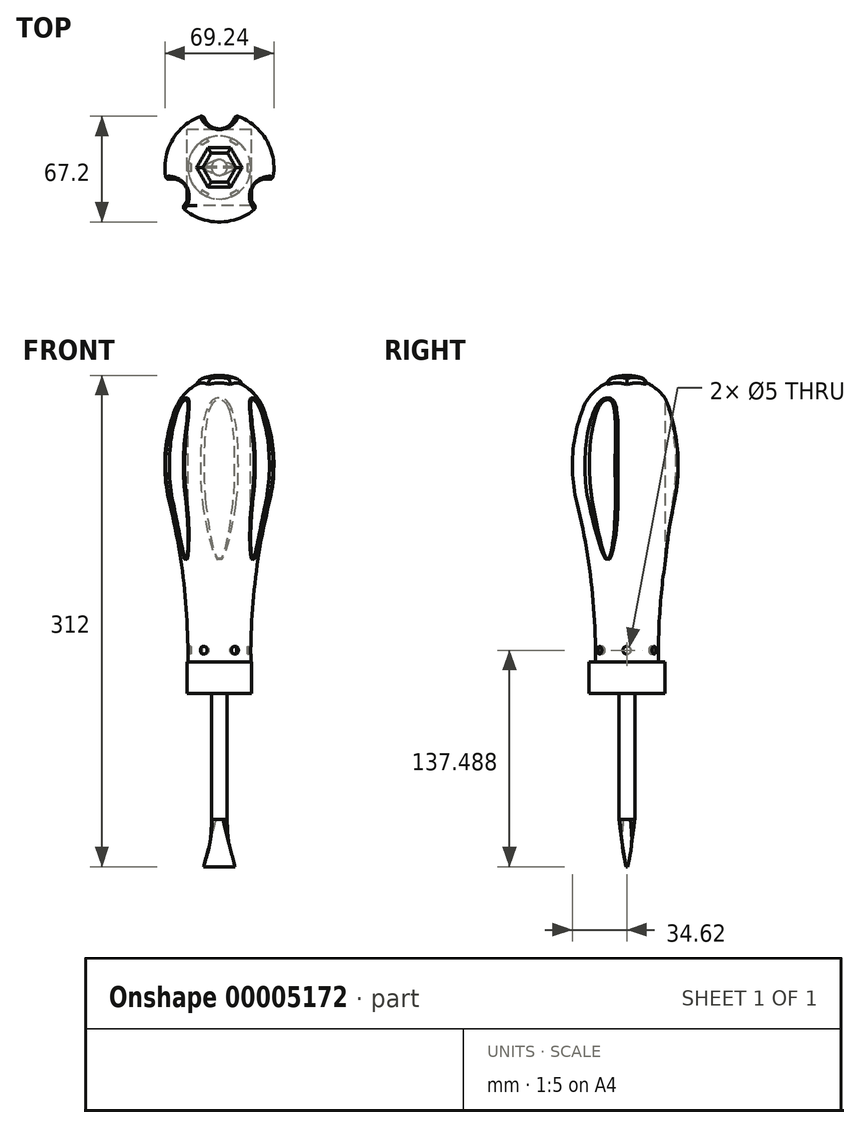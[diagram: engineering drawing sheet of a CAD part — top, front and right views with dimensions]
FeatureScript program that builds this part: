
annotation { "Feature Type Name" : "Feature", "Feature Type Description" : "" }
export const myFeature = defineFeature(function(context is Context, id is Id, definition is map)
    precondition{}
    {
        {
            var Q0;
            Q0=qCreatedBy(makeId("Front.planeOp"),FACE);
            var sketch = newSketch(context, id + "F0", { "sketchPlane" : qUnion([Q0])});
            skLineSegment(sketch, "E0", {"start": v(0, 0) * mm, "end": v(5, 0) * mm});
            skLineSegment(sketch, "E1", {"start": v(5, 0) * mm, "end": v(5, 99.99) * mm});
            skLineSegment(sketch, "E2", {"start": v(5, 99.99) * mm, "end": v(20, 99.99) * mm});
            skLineSegment(sketch, "E3", {"start": v(20, 99.99) * mm, "end": v(20, 104.99) * mm});
            skArc(sketch, "E4", {"start": v(20, 104.99) * mm, "mid": v(22.93, 153.35) * mm, "end": v(31.7, 201) * mm});
            skArc(sketch, "E5", {"start": v(31.7, 201) * mm, "mid": v(34.43, 231.14) * mm, "end": v(28.02, 260.71) * mm});
            skArc(sketch, "E6", {"start": v(28.02, 260.71) * mm, "mid": v(24.7, 267.02) * mm, "end": v(20, 272.36) * mm});
            skLineSegment(sketch, "E7", {"start": v(0, 280) * mm, "end": v(0, 0) * mm});
            skArc(sketch, "E8", {"start": v(20, 274.98) * mm, "mid": v(10.6, 280.2) * mm, "end": v(0, 282) * mm});
            skLineSegment(sketch, "E9", {"start": v(0, 280) * mm, "end": v(0, 282) * mm});
            skLineSegment(sketch, "E10", {"start": v(20, 272.36) * mm, "end": v(20, 274.98) * mm});
            skSolve(sketch);
        }
        {
            var Q0;
            Q0 = qSketchRegion(id + "F0", true);
            var Q1;
            Q1=sQuery(id+"F0.wireOp",EDGE,"E7");
            revolve(context, id + "F1", {"entities" : qUnion([Q0]), "axis" : qUnion([Q1]), "revolveType" : RevolveType.FULL});
        }
        {
            var Q0;
            Q0=qCreatedBy(makeId("Top.planeOp"),FACE);
            cPlane(context, id + "F2", {"entities" : qUnion([Q0]), "cplaneType" : CPlaneType.OFFSET, "offset" : 300 * mm, "width" : 150 * mm, "height" : 150 * mm});
        }
        {
            var Q0;
            Q0=qCreatedBy(id+"F2.planeOp",FACE);
            var sketch = newSketch(context, id + "F3", { "sketchPlane" : qUnion([Q0])});
            skCircle(sketch, "E11.cCircle", {"center": v(0, 0) * mm, "radius": 12.5 * mm, "construction": true});
            skLineSegment(sketch, "E11.0", {"start": v(7.22, 12.5) * mm, "end": v(14.43, 0) * mm});
            skLineSegment(sketch, "E11.1", {"start": v(14.43, 0) * mm, "end": v(7.22, -12.5) * mm});
            skLineSegment(sketch, "E11.2", {"start": v(7.22, -12.5) * mm, "end": v(-7.22, -12.5) * mm});
            skLineSegment(sketch, "E11.3", {"start": v(-7.22, -12.5) * mm, "end": v(-14.43, 0) * mm});
            skLineSegment(sketch, "E11.4", {"start": v(-14.43, 0) * mm, "end": v(-7.22, 12.5) * mm});
            skLineSegment(sketch, "E11.5", {"start": v(-7.22, 12.5) * mm, "end": v(7.22, 12.5) * mm});
            skPoint(sketch, "E11.0.midPoint", {"position": v(10.83, 6.25) * mm});
            skCircle(sketch, "E12.0", {"center": v(0, 0) * mm, "radius": 20 * mm});
            skSolve(sketch);
        }
        {
            var Q0;
            Q0=makeQuery(id+"F3.imprint","IMPRINT",FACE,{"disambiguationData":[TD([[makeQuery(id+"F3.imprint","IMPRINT",EDGE,{"derivedFrom":sQuery(id+"F3.wireOp",EDGE,"E11.0")}),1.0]])]});
            var Q1;
            Q1=makeQuery(id+"F1.opRevolve","SWEPT_FACE",FACE,{"disambiguationData":[OSD([sQuery(id+"F0.wireOp",EDGE,"E6")])]});
            extrude(context, id + "F4", {"entities" : qUnion([Q0]), "operationType" : NewBodyOperationType.REMOVE, "endBound" : BoundingType.UP_TO_SURFACE, "oppositeDirection" : true, "endBoundEntityFace" : qUnion([Q1]), "depth" : 25 * mm});
        }
        {
            var Q0;
            Q0=qCreatedBy(id+"F2.planeOp",FACE);
            var sketch = newSketch(context, id + "F5", { "sketchPlane" : qUnion([Q0])});
            skCircle(sketch, "E13", {"center": v(0, 34.5) * mm, "radius": 10 * mm});
            skSolve(sketch);
        }
        {
            var Q0;
            Q0 = qSketchRegion(id + "F5", true);
            extrude(context, id + "F6", {"entities" : qUnion([Q0]), "endBound" : BoundingType.THROUGH_ALL, "oppositeDirection" : true, "depth" : 25 * mm});
        }
        {
            var Q0;
            Q0=makeQuery(id+"F6.opExtrude","SWEPT_FACE",FACE,{"disambiguationData":[OSD([sQuery(id+"F5.wireOp",EDGE,"E13")])]});
            var Q1;
            Q1=makeQuery(id+"F6.opExtrude","SWEPT_BODY",BODY,{"disambiguationData":[OSD([sQuery(id+"F5.wireOp",EDGE,"E13")])]});
            var Q2;
            Q2=makeQuery(id+"F1.opRevolve","SWEPT_FACE",FACE,{"disambiguationData":[OSD([sQuery(id+"F0.wireOp",EDGE,"E5")])]});
            circularPattern(context, id + "F7", {"entities" : qUnion([Q1]), "axis" : qUnion([Q2]), "angle" : 360 * degree, "instanceCount" : 3, "equalSpace" : true});
        }
        {
            var Q0;
            Q0=makeQuery(id+"F7.opPattern","COPY",BODY,{"derivedFrom":makeQuery(id+"F6.opExtrude","SWEPT_BODY",BODY,{"disambiguationData":[OSD([sQuery(id+"F5.wireOp",EDGE,"E13")])]}),"instanceName":"3"});
            var Q1;
            Q1=makeQuery(id+"F7.opPattern","COPY",BODY,{"derivedFrom":makeQuery(id+"F6.opExtrude","SWEPT_BODY",BODY,{"disambiguationData":[OSD([sQuery(id+"F5.wireOp",EDGE,"E13")])]}),"instanceName":"4"});
            var Q2;
            Q2=makeQuery(id+"F7.opPattern","COPY",BODY,{"derivedFrom":makeQuery(id+"F6.opExtrude","SWEPT_BODY",BODY,{"disambiguationData":[OSD([sQuery(id+"F5.wireOp",EDGE,"E13")])]}),"instanceName":"5"});
            var Q3;
            Q3=makeQuery(id+"F6.opExtrude","SWEPT_BODY",BODY,{"disambiguationData":[OSD([sQuery(id+"F5.wireOp",EDGE,"E13")])]});
            var Q4;
            Q4=makeQuery(id+"F7.opPattern","COPY",BODY,{"derivedFrom":makeQuery(id+"F6.opExtrude","SWEPT_BODY",BODY,{"disambiguationData":[OSD([sQuery(id+"F5.wireOp",EDGE,"E13")])]}),"instanceName":"1"});
            var Q5;
            Q5=makeQuery(id+"F7.opPattern","COPY",BODY,{"derivedFrom":makeQuery(id+"F6.opExtrude","SWEPT_BODY",BODY,{"disambiguationData":[OSD([sQuery(id+"F5.wireOp",EDGE,"E13")])]}),"instanceName":"2"});
            var Q6;
            Q6=makeQuery(id+"F1.opRevolve","SWEPT_BODY",BODY,{"disambiguationData":[OSD([sQuery(id+"F0.wireOp",EDGE,"E0"),sQuery(id+"F0.wireOp",EDGE,"E1"),sQuery(id+"F0.wireOp",EDGE,"E2"),sQuery(id+"F0.wireOp",EDGE,"E3"),sQuery(id+"F0.wireOp",EDGE,"E4"),sQuery(id+"F0.wireOp",EDGE,"E5"),sQuery(id+"F0.wireOp",EDGE,"E6"),sQuery(id+"F0.wireOp",EDGE,"E7"),sQuery(id+"F0.wireOp",EDGE,"E8"),sQuery(id+"F0.wireOp",EDGE,"E9"),sQuery(id+"F0.wireOp",EDGE,"E10")])]});
            booleanBodies(context, id + "F8", {"operationType" : BooleanOperationType.SUBTRACTION, "tools" : qUnion([Q0, Q1, Q2, Q3, Q4, Q5]), "targets" : qUnion([Q6])});
        }
        {
            var Q0;
            Q0=makeQuery(id+"F8.opBoolean","INTERSECT",EDGE,{"disambiguationData":[OD(1.0)],"derivedFrom":[makeQuery(id+"F1.opRevolve","SWEPT_FACE",FACE,{"disambiguationData":[OSD([sQuery(id+"F0.wireOp",EDGE,"E5")])]}),makeQuery(id+"F6.opExtrude","SWEPT_FACE",FACE,{"disambiguationData":[OSD([sQuery(id+"F5.wireOp",EDGE,"E13")])]})]});
            var Q1;
            Q1=makeQuery(id+"F8.opBoolean","INTERSECT",EDGE,{"disambiguationData":[OD(0.0)],"derivedFrom":[makeQuery(id+"F1.opRevolve","SWEPT_FACE",FACE,{"disambiguationData":[OSD([sQuery(id+"F0.wireOp",EDGE,"E5")])]}),makeQuery(id+"F7.opPattern","COPY",FACE,{"derivedFrom":makeQuery(id+"F6.opExtrude","SWEPT_FACE",FACE,{"disambiguationData":[OSD([sQuery(id+"F5.wireOp",EDGE,"E13")])]}),"instanceName":"5"})]});
            var Q2;
            Q2=makeQuery(id+"F8.opBoolean","INTERSECT",EDGE,{"disambiguationData":[OD(1.0)],"derivedFrom":[makeQuery(id+"F1.opRevolve","SWEPT_FACE",FACE,{"disambiguationData":[OSD([sQuery(id+"F0.wireOp",EDGE,"E5")])]}),makeQuery(id+"F7.opPattern","COPY",FACE,{"derivedFrom":makeQuery(id+"F6.opExtrude","SWEPT_FACE",FACE,{"disambiguationData":[OSD([sQuery(id+"F5.wireOp",EDGE,"E13")])]}),"instanceName":"4"})]});
            var Q3;
            Q3=makeQuery(id+"F8.opBoolean","INTERSECT",EDGE,{"disambiguationData":[OD(1.0)],"derivedFrom":[makeQuery(id+"F1.opRevolve","SWEPT_FACE",FACE,{"disambiguationData":[OSD([sQuery(id+"F0.wireOp",EDGE,"E5")])]}),makeQuery(id+"F7.opPattern","COPY",FACE,{"derivedFrom":makeQuery(id+"F6.opExtrude","SWEPT_FACE",FACE,{"disambiguationData":[OSD([sQuery(id+"F5.wireOp",EDGE,"E13")])]}),"instanceName":"3"})]});
            var Q4;
            Q4=makeQuery(id+"F8.opBoolean","INTERSECT",EDGE,{"disambiguationData":[OD(1.0)],"derivedFrom":[makeQuery(id+"F1.opRevolve","SWEPT_FACE",FACE,{"disambiguationData":[OSD([sQuery(id+"F0.wireOp",EDGE,"E5")])]}),makeQuery(id+"F7.opPattern","COPY",FACE,{"derivedFrom":makeQuery(id+"F6.opExtrude","SWEPT_FACE",FACE,{"disambiguationData":[OSD([sQuery(id+"F5.wireOp",EDGE,"E13")])]}),"instanceName":"2"})]});
            var Q5;
            Q5=makeQuery(id+"F8.opBoolean","INTERSECT",EDGE,{"disambiguationData":[OD(1.0)],"derivedFrom":[makeQuery(id+"F1.opRevolve","SWEPT_FACE",FACE,{"disambiguationData":[OSD([sQuery(id+"F0.wireOp",EDGE,"E5")])]}),makeQuery(id+"F7.opPattern","COPY",FACE,{"derivedFrom":makeQuery(id+"F6.opExtrude","SWEPT_FACE",FACE,{"disambiguationData":[OSD([sQuery(id+"F5.wireOp",EDGE,"E13")])]}),"instanceName":"1"})]});
            fillet(context, id + "F9", {"entities" : qUnion([Q0, Q1, Q2, Q3, Q4, Q5]), "radius" : 2 * mm, "tangentPropagation" : true, "allowEdgeOverflow" : false});
        }
        {
            var Q0;
            Q0=qCreatedBy(makeId("Top.planeOp"),FACE);
            cPlane(context, id + "F10", {"entities" : qUnion([Q0]), "cplaneType" : CPlaneType.OFFSET, "offset" : 15 * mm, "oppositeDirection" : true, "width" : 150 * mm, "height" : 150 * mm});
        }
        {
            var Q0;
            Q0=qCreatedBy(id+"F10.planeOp",FACE);
            var sketch = newSketch(context, id + "F11", { "sketchPlane" : qUnion([Q0])});
            skLineSegment(sketch, "E14.rect.bottom", {"start": v(6, 3) * mm, "end": v(-6, 3) * mm});
            skLineSegment(sketch, "E14.rect.top", {"start": v(6, -3) * mm, "end": v(-6, -3) * mm});
            skLineSegment(sketch, "E14.rect.left", {"start": v(6, 3) * mm, "end": v(6, -3) * mm});
            skLineSegment(sketch, "E14.rect.right", {"start": v(-6, 3) * mm, "end": v(-6, -3) * mm});
            skPoint(sketch, "E14.rect.middle", {"position": v(0, 0) * mm});
            skSolve(sketch);
        }
        {
            var Q0;
            Q0=qCreatedBy(id+"F10.planeOp",FACE);
            cPlane(context, id + "F12", {"entities" : qUnion([Q0]), "cplaneType" : CPlaneType.OFFSET, "offset" : 15 * mm, "oppositeDirection" : true, "width" : 150 * mm, "height" : 150 * mm});
        }
        {
            var Q0;
            Q0=qCreatedBy(id+"F12.planeOp",FACE);
            var sketch = newSketch(context, id + "F13", { "sketchPlane" : qUnion([Q0])});
            skLineSegment(sketch, "E15.rect.bottom", {"start": v(10, 0.5) * mm, "end": v(-10, 0.5) * mm});
            skLineSegment(sketch, "E15.rect.top", {"start": v(10, -0.5) * mm, "end": v(-10, -0.5) * mm});
            skLineSegment(sketch, "E15.rect.left", {"start": v(10, 0.5) * mm, "end": v(10, -0.5) * mm});
            skLineSegment(sketch, "E15.rect.right", {"start": v(-10, 0.5) * mm, "end": v(-10, -0.5) * mm});
            skPoint(sketch, "E15.rect.middle", {"position": v(0, 0) * mm});
            skSolve(sketch);
        }
        {
            var Q0;
            Q0=makeQuery(id+"F1.opRevolve","SWEPT_FACE",FACE,{"disambiguationData":[OSD([sQuery(id+"F0.wireOp",EDGE,"E0")])]});
            var Q1;
            Q1=makeQuery(id+"F11.imprint","IMPRINT",FACE,{"disambiguationData":[TD([[makeQuery(id+"F11.imprint","IMPRINT",EDGE,{"derivedFrom":sQuery(id+"F11.wireOp",EDGE,"E14.rect.bottom")}),1.0]])]});
            var Q2;
            Q2=makeQuery(id+"F13.imprint","IMPRINT",FACE,{"disambiguationData":[TD([[makeQuery(id+"F13.imprint","IMPRINT",EDGE,{"derivedFrom":sQuery(id+"F13.wireOp",EDGE,"E15.rect.bottom")}),1.0]])]});
            loft(context, id + "F14", {"operationType" : NewBodyOperationType.ADD, "sheetProfilesArray" : [{ "sheetProfileEntities" : qUnion([Q0]) }, { "sheetProfileEntities" : qUnion([Q1]) }, { "sheetProfileEntities" : qUnion([Q2]) }]});
        }
        {
            var Q0;
            Q0=qCreatedBy(makeId("Right.planeOp"),FACE);
            cPlane(context, id + "F15", {"entities" : qUnion([Q0]), "cplaneType" : CPlaneType.OFFSET, "offset" : 150 * mm, "width" : 150 * mm, "height" : 150 * mm});
        }
        {
            var Q0;
            Q0=qCreatedBy(id+"F15.planeOp",FACE);
            var sketch = newSketch(context, id + "F16", { "sketchPlane" : qUnion([Q0])});
            skCircle(sketch, "E16", {"center": v(0, 107.49) * mm, "radius": 2.5 * mm});
            skSolve(sketch);
        }
        {
            var Q0;
            Q0 = qSketchRegion(id + "F16", true);
            var Q1;
            Q1=makeQuery(id+"F1.opRevolve","SWEPT_FACE",FACE,{"disambiguationData":[OSD([sQuery(id+"F0.wireOp",EDGE,"E4")])]});
            extrude(context, id + "F17", {"entities" : qUnion([Q0]), "endBound" : BoundingType.UP_TO_SURFACE, "oppositeDirection" : true, "endBoundEntityFace" : qUnion([Q1]), "depth" : 25 * mm});
        }
        {
            var Q0;
            Q0=makeQuery(id+"F17.opExtrude","SWEPT_FACE",FACE,{"disambiguationData":[OSD([sQuery(id+"F16.wireOp",EDGE,"E16")])]});
            var Q1;
            Q1=makeQuery(id+"F17.opExtrude","SWEPT_BODY",BODY,{"disambiguationData":[OSD([sQuery(id+"F16.wireOp",EDGE,"E16")])]});
            var Q2;
            Q2=makeQuery(id+"F1.opRevolve","SWEPT_FACE",FACE,{"disambiguationData":[OSD([sQuery(id+"F0.wireOp",EDGE,"E4")])]});
            circularPattern(context, id + "F18", {"entities" : qUnion([Q1]), "axis" : qUnion([Q2]), "angle" : 360 * degree, "instanceCount" : 6, "equalSpace" : true});
        }
        {
            var Q0;
            Q0=makeQuery(id+"F18.opPattern","COPY",BODY,{"derivedFrom":makeQuery(id+"F17.opExtrude","SWEPT_BODY",BODY,{"disambiguationData":[OSD([sQuery(id+"F16.wireOp",EDGE,"E16")])]}),"instanceName":"3"});
            var Q1;
            Q1=makeQuery(id+"F18.opPattern","COPY",BODY,{"derivedFrom":makeQuery(id+"F17.opExtrude","SWEPT_BODY",BODY,{"disambiguationData":[OSD([sQuery(id+"F16.wireOp",EDGE,"E16")])]}),"instanceName":"4"});
            var Q2;
            Q2=makeQuery(id+"F18.opPattern","COPY",BODY,{"derivedFrom":makeQuery(id+"F17.opExtrude","SWEPT_BODY",BODY,{"disambiguationData":[OSD([sQuery(id+"F16.wireOp",EDGE,"E16")])]}),"instanceName":"5"});
            var Q3;
            Q3=makeQuery(id+"F17.opExtrude","SWEPT_BODY",BODY,{"disambiguationData":[OSD([sQuery(id+"F16.wireOp",EDGE,"E16")])]});
            var Q4;
            Q4=makeQuery(id+"F18.opPattern","COPY",BODY,{"derivedFrom":makeQuery(id+"F17.opExtrude","SWEPT_BODY",BODY,{"disambiguationData":[OSD([sQuery(id+"F16.wireOp",EDGE,"E16")])]}),"instanceName":"1"});
            var Q5;
            Q5=makeQuery(id+"F18.opPattern","COPY",BODY,{"derivedFrom":makeQuery(id+"F17.opExtrude","SWEPT_BODY",BODY,{"disambiguationData":[OSD([sQuery(id+"F16.wireOp",EDGE,"E16")])]}),"instanceName":"2"});
            var Q6;
            Q6=makeQuery(id+"F1.opRevolve","SWEPT_BODY",BODY,{"disambiguationData":[OSD([sQuery(id+"F0.wireOp",EDGE,"E0"),sQuery(id+"F0.wireOp",EDGE,"E1"),sQuery(id+"F0.wireOp",EDGE,"E2"),sQuery(id+"F0.wireOp",EDGE,"E3"),sQuery(id+"F0.wireOp",EDGE,"E4"),sQuery(id+"F0.wireOp",EDGE,"E5"),sQuery(id+"F0.wireOp",EDGE,"E6"),sQuery(id+"F0.wireOp",EDGE,"E7"),sQuery(id+"F0.wireOp",EDGE,"E8"),sQuery(id+"F0.wireOp",EDGE,"E9"),sQuery(id+"F0.wireOp",EDGE,"E10")])]});
            var Q7;
            Q7=makeQuery(id+"F18.opPattern","COPY",FACE,{"derivedFrom":makeQuery(id+"F17.opExtrude","CAP_FACE",FACE,{"disambiguationData":[OSD([sQuery(id+"F16.wireOp",EDGE,"E16")])],"isStart":false}),"instanceName":"5"});
            var Q8;
            Q8=makeQuery(id+"F18.opPattern","COPY",FACE,{"derivedFrom":makeQuery(id+"F17.opExtrude","CAP_FACE",FACE,{"disambiguationData":[OSD([sQuery(id+"F16.wireOp",EDGE,"E16")])],"isStart":false}),"instanceName":"4"});
            var Q9;
            Q9=makeQuery(id+"F18.opPattern","COPY",FACE,{"derivedFrom":makeQuery(id+"F17.opExtrude","CAP_FACE",FACE,{"disambiguationData":[OSD([sQuery(id+"F16.wireOp",EDGE,"E16")])],"isStart":false}),"instanceName":"3"});
            var Q10;
            Q10=makeQuery(id+"F18.opPattern","COPY",FACE,{"derivedFrom":makeQuery(id+"F17.opExtrude","CAP_FACE",FACE,{"disambiguationData":[OSD([sQuery(id+"F16.wireOp",EDGE,"E16")])],"isStart":false}),"instanceName":"2"});
            var Q11;
            Q11=makeQuery(id+"F18.opPattern","COPY",FACE,{"derivedFrom":makeQuery(id+"F17.opExtrude","CAP_FACE",FACE,{"disambiguationData":[OSD([sQuery(id+"F16.wireOp",EDGE,"E16")])],"isStart":false}),"instanceName":"1"});
            var Q12;
            Q12=makeQuery(id+"F17.opExtrude","CAP_FACE",FACE,{"disambiguationData":[OSD([sQuery(id+"F16.wireOp",EDGE,"E16")])],"isStart":false});
            booleanBodies(context, id + "F19", {"operationType" : BooleanOperationType.SUBTRACTION, "tools" : qUnion([Q0, Q1, Q2, Q3, Q4, Q5]), "targets" : qUnion([Q6]), "offset" : true, "entitiesToOffset" : qUnion([Q7, Q8, Q9, Q10, Q11, Q12]), "offsetDistance" : 2 * mm});
        }
        {
            var Q0;
            Q0=qCreatedBy(makeId("Front.planeOp"),FACE);
            var sketch = newSketch(context, id + "F20", { "sketchPlane" : qUnion([Q0])});
            skLineSegment(sketch, "E17", {"start": v(-10, 99.99) * mm, "end": v(-10, 97.99) * mm});
            skLineSegment(sketch, "E18", {"start": v(-7, 94.99) * mm, "end": v(7, 94.99) * mm});
            skLineSegment(sketch, "E19", {"start": v(10, 97.99) * mm, "end": v(10, 99.99) * mm});
            skLineSegment(sketch, "E20", {"start": v(10, 99.99) * mm, "end": v(-10, 99.99) * mm});
            skPoint(sketch, "E21.visualSharp", {"position": v(-10, 94.99) * mm});
            skArc(sketch, "E21.filletArc", {"start": v(-10, 97.99) * mm, "mid": v(-9.12, 95.87) * mm, "end": v(-7, 94.99) * mm});
            skPoint(sketch, "E22.visualSharp", {"position": v(10, 94.99) * mm});
            skArc(sketch, "E22.filletArc", {"start": v(7, 94.99) * mm, "mid": v(9.12, 95.87) * mm, "end": v(10, 97.99) * mm});
            skSolve(sketch);
        }
        {
            var Q0;
            Q0 = qSketchRegion(id + "F20", true);
            extrude(context, id + "F21", {"entities" : qUnion([Q0]), "operationType" : NewBodyOperationType.ADD, "endBound" : BoundingType.SYMMETRIC, "depth" : 2 * mm});
        }
        {
            var Q0;
            Q0=makeQuery(id+"F4.boolean.opBoolean","INTERSECT",EDGE,{"derivedFrom":[makeQuery(id+"F1.opRevolve","SWEPT_FACE",FACE,{"disambiguationData":[OSD([sQuery(id+"F0.wireOp",EDGE,"E8")])]}),makeQuery(id+"F4.opExtrude","SWEPT_FACE",FACE,{"disambiguationData":[OSD([sQuery(id+"F3.wireOp",EDGE,"E11.1")])]})]});
            var Q1;
            Q1=makeQuery(id+"F4.boolean.opBoolean","INTERSECT",EDGE,{"derivedFrom":[makeQuery(id+"F1.opRevolve","SWEPT_FACE",FACE,{"disambiguationData":[OSD([sQuery(id+"F0.wireOp",EDGE,"E8")])]}),makeQuery(id+"F4.opExtrude","SWEPT_FACE",FACE,{"disambiguationData":[OSD([sQuery(id+"F3.wireOp",EDGE,"E11.2")])]})]});
            var Q2;
            Q2=makeQuery(id+"F4.boolean.opBoolean","INTERSECT",EDGE,{"derivedFrom":[makeQuery(id+"F1.opRevolve","SWEPT_FACE",FACE,{"disambiguationData":[OSD([sQuery(id+"F0.wireOp",EDGE,"E8")])]}),makeQuery(id+"F4.opExtrude","SWEPT_FACE",FACE,{"disambiguationData":[OSD([sQuery(id+"F3.wireOp",EDGE,"E11.3")])]})]});
            var Q3;
            Q3=makeQuery(id+"F4.boolean.opBoolean","INTERSECT",EDGE,{"derivedFrom":[makeQuery(id+"F1.opRevolve","SWEPT_FACE",FACE,{"disambiguationData":[OSD([sQuery(id+"F0.wireOp",EDGE,"E8")])]}),makeQuery(id+"F4.opExtrude","SWEPT_FACE",FACE,{"disambiguationData":[OSD([sQuery(id+"F3.wireOp",EDGE,"E11.0")])]})]});
            var Q4;
            Q4=makeQuery(id+"F4.boolean.opBoolean","INTERSECT",EDGE,{"derivedFrom":[makeQuery(id+"F1.opRevolve","SWEPT_FACE",FACE,{"disambiguationData":[OSD([sQuery(id+"F0.wireOp",EDGE,"E8")])]}),makeQuery(id+"F4.opExtrude","SWEPT_FACE",FACE,{"disambiguationData":[OSD([sQuery(id+"F3.wireOp",EDGE,"E11.5")])]})]});
            var Q5;
            Q5=makeQuery(id+"F4.boolean.opBoolean","INTERSECT",EDGE,{"derivedFrom":[makeQuery(id+"F1.opRevolve","SWEPT_FACE",FACE,{"disambiguationData":[OSD([sQuery(id+"F0.wireOp",EDGE,"E8")])]}),makeQuery(id+"F4.opExtrude","SWEPT_FACE",FACE,{"disambiguationData":[OSD([sQuery(id+"F3.wireOp",EDGE,"E11.4")])]})]});
            fillet(context, id + "F22", {"entities" : qUnion([Q0, Q1, Q2, Q3, Q4, Q5]), "radius" : 5 * mm, "tangentPropagation" : true, "allowEdgeOverflow" : false});
        }
        {
            var Q0;
            Q0=makeQuery(id+"F1.opRevolve","SWEPT_FACE",FACE,{"disambiguationData":[OSD([sQuery(id+"F0.wireOp",EDGE,"E2")])]});
            var sketch = newSketch(context, id + "F23", { "sketchPlane" : qUnion([Q0])});
            skLineSegment(sketch, "E23.bottom", {"start": v(20.45, 24.2) * mm, "end": v(-20.45, 24.2) * mm});
            skLineSegment(sketch, "E23.top", {"start": v(20.45, -24.2) * mm, "end": v(-20.45, -24.2) * mm});
            skLineSegment(sketch, "E23.left", {"start": v(20.45, 24.2) * mm, "end": v(20.45, -24.2) * mm});
            skLineSegment(sketch, "E23.right", {"start": v(-20.45, 24.2) * mm, "end": v(-20.45, -24.2) * mm});
            skSolve(sketch);
        }
        {
            var Q0;
            Q0 = qSketchRegion(id + "F23", true);
            extrude(context, id + "F24", {"entities" : qUnion([Q0]), "operationType" : NewBodyOperationType.ADD, "depth" : 20 * mm, "offsetDistance" : 25 * mm});
        }
    });
